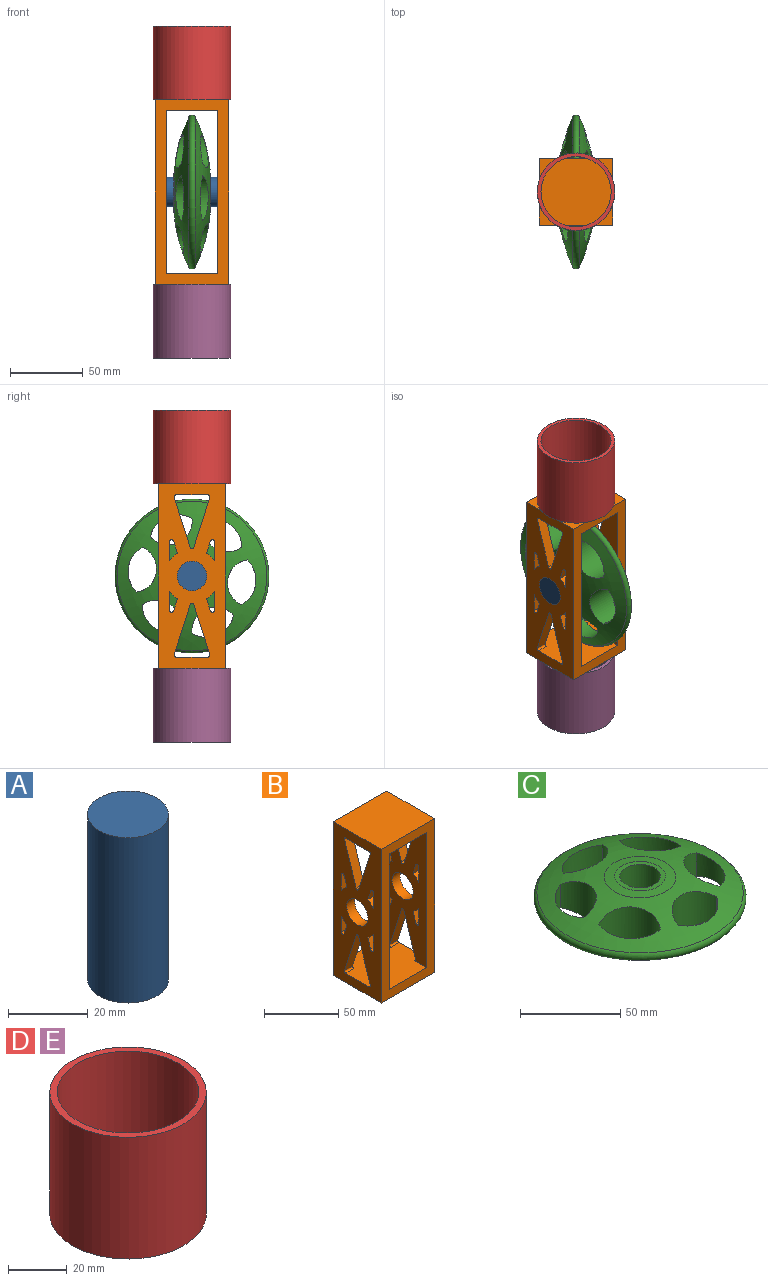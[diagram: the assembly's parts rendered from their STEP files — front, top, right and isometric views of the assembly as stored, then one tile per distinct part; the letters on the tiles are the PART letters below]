
ASSEMBLY  parts=5 mates=4
PART A: 3 faces, bbox 20.3x20.3x50.8 mm
  f0: cylinder r=10.16mm len=50.8mm, axis (0,0,1), area 3242.9mm2, adj f1,f2
  f1: plane 20.32x20.32mm, normal (0,0,-1), area 324.3mm2, adj f0
  f2: plane 20.32x20.32mm, normal (0,0,1), area 324.3mm2, adj f0
PART B: 68 faces, bbox 50.8x45.7x127 mm
  f0: plane 127x45.72mm, normal (-1,0,0), area 4280.4mm2, adj f4,f5,f6,f7,f8,f9,f39,f40
  f1: plane 111.76x45.72mm, normal (1,0,0), area 3583.6mm2, adj f6,f7,f8,f9,f39,f40,f41,f42
  f2: plane 111.76x45.72mm, normal (-1,0,0), area 3583.6mm2, adj f6,f7,f8,f9,f10,f11,f12,f13
  f3: plane 127x45.72mm, normal (1,0,0), area 4280.4mm2, adj f4,f5,f6,f7,f8,f9,f10,f11
  f4: plane 50.8x45.72mm, normal (0,0,1), area 2322.6mm2, adj f0,f3,f8,f9
  f5: plane 50.8x45.72mm, normal (0,0,-1), area 2322.6mm2, adj f0,f3,f8,f9
  f6: plane 50.8x45.72mm, normal (0,0,-1), area 1963.2mm2, adj f0,f1,f2,f3,f8,f9,f15,f20
  f7: plane 50.8x45.72mm, normal (0,0,1), area 1963.2mm2, adj f0,f1,f2,f3,f8,f9,f25,f30
  f8: plane 127x50.8mm, normal (0,-1,0), area 2477.4mm2, adj f0,f1,f2,f3,f4,f5,f6,f7
  f9: plane 127x50.8mm, normal (0,1,0), area 2477.4mm2, adj f0,f1,f2,f3,f4,f5,f6,f7
  f10: cylinder r=10.16mm len=20.32mm, axis (-1,0,0), area 486.4mm2, adj f2,f3
  f11: plane 13.13x7.62mm, normal (0,1,0), area 100mm2, adj f2,f3,f12,f14
  f12: cylinder r=18.63mm len=7.62mm, axis (-1,0,0), area 55.2mm2, adj f2,f3,f11,f13
  f13: plane 8.54x7.62mm, normal (0,-0.95,-0.3), area 68.3mm2, adj f2,f3,f12,f14
  f14: cylinder r=1.27mm len=7.62mm, axis (-1,0,0), area 27.4mm2, adj f2,f3,f11,f13
  f15: cylinder r=1.27mm len=7.62mm, axis (-1,0,0), area 18.2mm2, adj f2,f3,f6,f16
  f16: plane 34.71x11.08mm, normal (0,0.95,0.3), area 277.6mm2, adj f2,f3,f15,f17
  f17: cylinder r=1.27mm len=7.62mm, axis (-1,0,0), area 12.2mm2, adj f2,f3,f16,f18
  f18: cylinder r=1.27mm len=7.62mm, axis (-1,0,0), area 12.1mm2, adj f2,f3,f17,f19
  f19: plane 34.71x11.08mm, normal (0,-0.95,0.3), area 277.6mm2, adj f2,f3,f18,f20
  f20: cylinder r=1.27mm len=7.62mm, axis (-1,0,0), area 18.2mm2, adj f2,f3,f6,f19
  f21: cylinder r=18.63mm len=7.62mm, axis (-1,0,0), area 55.2mm2, adj f2,f3,f22,f24
  f22: plane 8.54x7.62mm, normal (0,0.95,0.3), area 68.3mm2, adj f2,f3,f21,f23
  f23: cylinder r=1.27mm len=7.62mm, axis (-1,0,0), area 27.4mm2, adj f2,f3,f22,f24
  f24: plane 13.13x7.62mm, normal (0,-1,0), area 100mm2, adj f2,f3,f21,f23
  f25: cylinder r=1.27mm len=7.62mm, axis (-1,0,0), area 18.2mm2, adj f2,f3,f7,f26
  f26: plane 34.71x11.08mm, normal (0,-0.95,-0.3), area 277.6mm2, adj f2,f3,f25,f27
  f27: cylinder r=1.27mm len=7.62mm, axis (-1,0,0), area 12.1mm2, adj f2,f3,f26,f28
  f28: cylinder r=1.27mm len=7.62mm, axis (-1,0,0), area 12.2mm2, adj f2,f3,f27,f29
  f29: plane 34.71x11.08mm, normal (0,0.95,-0.3), area 277.6mm2, adj f2,f3,f28,f30
  f30: cylinder r=1.27mm len=7.62mm, axis (-1,0,0), area 18.2mm2, adj f2,f3,f7,f29
  f31: plane 8.54x7.62mm, normal (0,0.95,-0.3), area 68.3mm2, adj f2,f3,f32,f34
  f32: cylinder r=18.63mm len=7.62mm, axis (-1,0,0), area 55.2mm2, adj f2,f3,f31,f33
  f33: plane 13.13x7.62mm, normal (0,-1,0), area 100mm2, adj f2,f3,f32,f34
  f34: cylinder r=1.27mm len=7.62mm, axis (-1,0,0), area 27.4mm2, adj f2,f3,f31,f33
  f35: cylinder r=18.63mm len=7.62mm, axis (-1,0,0), area 55.2mm2, adj f2,f3,f36,f38
  f36: plane 13.13x7.62mm, normal (0,1,0), area 100mm2, adj f2,f3,f35,f37
  f37: cylinder r=1.27mm len=7.62mm, axis (-1,0,0), area 27.4mm2, adj f2,f3,f36,f38
  f38: plane 8.54x7.62mm, normal (0,-0.95,0.3), area 68.3mm2, adj f2,f3,f35,f37
  f39: cylinder r=10.16mm len=20.32mm, axis (-1,0,0), area 486.4mm2, adj f0,f1
  f40: cylinder r=1.27mm len=7.62mm, axis (-1,0,0), area 27.4mm2, adj f0,f1,f41,f43
  f41: plane 8.54x7.62mm, normal (0,-0.95,-0.3), area 68.3mm2, adj f0,f1,f40,f42
  f42: cylinder r=18.63mm len=7.62mm, axis (-1,0,0), area 55.2mm2, adj f0,f1,f41,f43
  f43: plane 13.13x7.62mm, normal (0,1,0), area 100mm2, adj f0,f1,f40,f42
  f44: cylinder r=1.27mm len=7.62mm, axis (-1,0,0), area 18.2mm2, adj f0,f1,f6,f45
  f45: plane 34.71x11.08mm, normal (0,-0.95,0.3), area 277.6mm2, adj f0,f1,f44,f46
  f46: cylinder r=1.27mm len=7.62mm, axis (-1,0,0), area 12.1mm2, adj f0,f1,f45,f47
  f47: cylinder r=1.27mm len=7.62mm, axis (-1,0,0), area 12.2mm2, adj f0,f1,f46,f48
  f48: plane 34.71x11.08mm, normal (0,0.95,0.3), area 277.6mm2, adj f0,f1,f47,f49
  f49: cylinder r=1.27mm len=7.62mm, axis (-1,0,0), area 18.2mm2, adj f0,f1,f6,f48
  f50: plane 13.13x7.62mm, normal (0,-1,0), area 100mm2, adj f0,f1,f51,f53
  f51: cylinder r=1.27mm len=7.62mm, axis (-1,0,0), area 27.4mm2, adj f0,f1,f50,f52
  f52: plane 8.54x7.62mm, normal (0,0.95,0.3), area 68.3mm2, adj f0,f1,f51,f53
  f53: cylinder r=18.63mm len=7.62mm, axis (-1,0,0), area 55.2mm2, adj f0,f1,f50,f52
  f54: cylinder r=1.27mm len=7.62mm, axis (-1,0,0), area 18.2mm2, adj f0,f1,f7,f55
  f55: plane 34.71x11.08mm, normal (0,0.95,-0.3), area 277.6mm2, adj f0,f1,f54,f56
  f56: cylinder r=1.27mm len=7.62mm, axis (-1,0,0), area 12.2mm2, adj f0,f1,f55,f57
  f57: cylinder r=1.27mm len=7.62mm, axis (-1,0,0), area 12.1mm2, adj f0,f1,f56,f58
  f58: plane 34.71x11.08mm, normal (0,-0.95,-0.3), area 277.6mm2, adj f0,f1,f57,f59
  f59: cylinder r=1.27mm len=7.62mm, axis (-1,0,0), area 18.2mm2, adj f0,f1,f7,f58
  f60: cylinder r=1.27mm len=7.62mm, axis (-1,0,0), area 27.4mm2, adj f0,f1,f61,f63
  f61: plane 13.13x7.62mm, normal (0,-1,0), area 100mm2, adj f0,f1,f60,f62
  f62: cylinder r=18.63mm len=7.62mm, axis (-1,0,0), area 55.2mm2, adj f0,f1,f61,f63
  f63: plane 8.54x7.62mm, normal (0,0.95,-0.3), area 68.3mm2, adj f0,f1,f60,f62
  f64: plane 8.54x7.62mm, normal (0,-0.95,0.3), area 68.3mm2, adj f0,f1,f65,f67
  f65: cylinder r=1.27mm len=7.62mm, axis (-1,0,0), area 27.4mm2, adj f0,f1,f64,f66
  f66: plane 13.13x7.62mm, normal (0,1,0), area 100mm2, adj f0,f1,f65,f67
  f67: cylinder r=18.63mm len=7.62mm, axis (-1,0,0), area 55.2mm2, adj f0,f1,f64,f66
PART C: 20 faces, bbox 114.6x114.6x25.4 mm
  f0: plane 25.4x25.4mm, normal (0,0,1), area 182.4mm2, adj f1,f7
  f1: cone r=17.89mm half-angle=83.6deg, axis (0,0,-1), area 502.4mm2, adj f0,f2
  f2: torus R=6.61mm, axis (0,0,1), area 4998.3mm2, adj f1,f3,f8,f9,f10,f11,f12,f13
  f3: torus R=50.4mm, axis (0,0,1), area 1863mm2, adj f2,f4
  f4: torus R=6.61mm, axis (0,0,1), area 4999.6mm2, adj f3,f5,f8,f9,f10,f11,f12,f13
  f5: cone r=17.89mm half-angle=83.6deg, axis (0,0,1), area 502.4mm2, adj f4,f6
  f6: plane 25.4x25.4mm, normal (0,0,-1), area 182.4mm2, adj f5,f7
  f7: cylinder r=10.16mm len=25.4mm, axis (0,0,1), area 1621.5mm2, adj f0,f6
  f8: cylinder r=16.25mm len=25.99mm, axis (0,0,1), area 818.1mm2, adj f2,f4,f9
  f9: cylinder r=19.47mm len=24.97mm, axis (0,0,1), area 443.1mm2, adj f2,f4,f8
  f10: cylinder r=16.25mm len=30.96mm, axis (0,0,1), area 818.1mm2, adj f2,f4,f11
  f11: cylinder r=19.47mm len=30.96mm, axis (0,0,1), area 443.1mm2, adj f2,f4,f10
  f12: cylinder r=16.25mm len=25.99mm, axis (0,0,1), area 818.1mm2, adj f2,f4,f13
  f13: cylinder r=19.47mm len=24.97mm, axis (0,0,1), area 443.1mm2, adj f2,f4,f12
  f14: cylinder r=16.25mm len=28.78mm, axis (0,0,1), area 818mm2, adj f2,f4,f15
  f15: cylinder r=19.47mm len=28.66mm, axis (0,0,1), area 443.1mm2, adj f2,f4,f14
  f16: cylinder r=16.25mm len=30.96mm, axis (0,0,1), area 818.1mm2, adj f2,f4,f17
  f17: cylinder r=19.47mm len=30.96mm, axis (0,0,1), area 443.1mm2, adj f2,f4,f16
  f18: cylinder r=16.25mm len=28.78mm, axis (0,0,1), area 818.1mm2, adj f2,f4,f19
  f19: cylinder r=19.47mm len=28.66mm, axis (0,0,1), area 443.1mm2, adj f2,f4,f18
PART D: 4 faces, bbox 53.3x53.3x50.8 mm
  f0: cylinder r=26.67mm len=53.34mm, axis (0,0,1), area 8512.7mm2, adj f1,f3
  f1: plane 53.34x53.34mm, normal (0,0,1), area 405.4mm2, adj f0,f2
  f2: cylinder r=24.13mm len=50.8mm, axis (0,0,1), area 7702mm2, adj f1,f3
  f3: plane 53.34x53.34mm, normal (0,0,-1), area 405.4mm2, adj f0,f2
PART E: same geometry as D
PLACE A rot(axis=(0,1,0),90deg) t=(-103.21,-2.81,-51.34)mm
PLACE B rot(axis=(0,1,0),180deg) t=(-109.56,-2.81,-114.84)mm
PLACE C rot(axis=(0,1,0),90deg) t=(-109.56,-2.81,-51.34)mm
PLACE D rot(axis=(0,1,0),180deg) t=(-109.56,-2.81,-114.84)mm
PLACE E rot(axis=(0,1,0),180deg) t=(-109.56,-2.81,-292.64)mm
MATE revolute B.f10 <-> A.f0  axis (-1,0,0) through (-134.96,-2.81,-51.34)mm
MATE revolute C.f7 <-> A.f0  axis (1,0,0) through (-109.56,-2.81,-51.34)mm
MATE fastened B.f4 <-> E.f0  axis (0,0,-1) through (-109.56,-2.81,-114.84)mm
MATE fastened D.f0 <-> B.f5  axis (0,0,-1) through (-109.56,-2.81,12.16)mm
